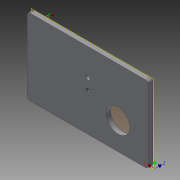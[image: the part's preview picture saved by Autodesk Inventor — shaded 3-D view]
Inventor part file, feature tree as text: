
AUTODESK INVENTOR PART (.ipt)
format: ipt  version: 2015 SP1 (Build 190203100, 203)  size: 2,543,104 bytes
history: native  units: in
note: dims shown in document units (in); Inventor stores cm internally (conversion verified against a paired STEP export)
features: sketch x4, extrude x4, hole x2, plane x1, fillet x1, reference x1
ambient origin geometry x8: Origin, YZ Plane, XZ Plane, XY Plane, X Axis, Y Axis, Z Axis, Center Point
bodies: Solid1 (feature_tree)
feature tree (13):
  plane  "Work Plane1"
  sketch  "Sketch1"  dims[d2=4.2323in d3=2.6575in d4=0.315in d5=0.0in]
  extrude  "Extrusion1"  Depth=0.315in
  fillet  "Fillet1"  Radius=0.315in
  extrude  "Extrusion2"  Depth=0.1181in TaperAngle=0.0deg
  extrude  "Extrusion3"  Depth=0.1181in TaperAngle=0.0deg
  hole  "Hole1"  [1 undecoded]
  extrude  "Extrusion4"  Depth=0.315in
  hole  "Hole2"  [1 undecoded]
  reference  "Reference1"
  sketch  "Sketch2"  dims[d6=0.1969in d7=0.1181in d8=0.0in]
  sketch  "Sketch3"  dims[d9=2.6575in d10=4.2323in]
  sketch  "Sketch4"  dims[d11=0.2617in d12=0.6299in d13=0.1575in d14=0.0787in d15=90.0deg d16=0.874in d17=0.8108in d18=0.1181in d19=0.0in d20=2.9134in d21=1.1811in d22=1.1811in d23=0.5906in d24=1.5748in d25=1.5748in d26=0.1969in d27=1.6535in d28=0.3937in d29=0.0in d30=4.2323in d31=3.4449in d32=0.315in d33=0.2362in d34=0.1575in d35=0.0787in d36=90.0deg d37=0.315in d38=0.8108in]
note: 2 required parameter values undecoded (feature->parameter linkage not recoverable at this tier; creation-order binding heuristic only, values carry confidence <= 0.55)
